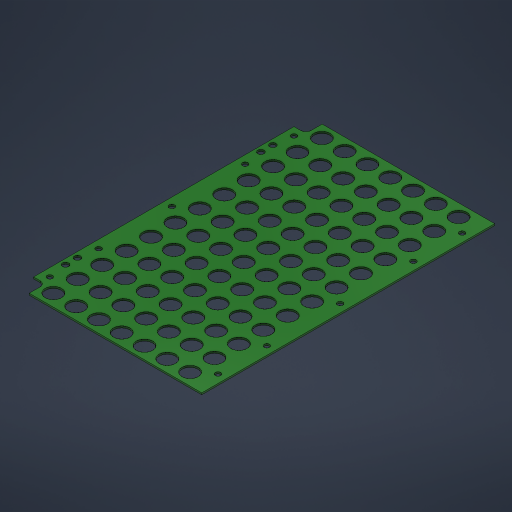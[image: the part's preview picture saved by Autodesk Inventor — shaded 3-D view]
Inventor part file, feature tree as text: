
AUTODESK INVENTOR PART (.ipt)
format: ipt  version: 2023.5 (Build 275446000, 446)  size: 413,696 bytes
history: native  units: mm
features: extrude x2, sketch x2
ambient origin geometry x8: Origin, YZ Plane, XZ Plane, XY Plane, X Axis, Y Axis, Z Axis, Center Point
bodies: Volumenkörper1 (feature_tree)
feature tree (4):
  extrude  "Extrusion1"  Depth=1.6mm
  extrude  "Extrusion2"  Depth=5.0mm
  sketch  "Skizze1"  dims[d0=1.6mm d1=0.0mm d2=5.7mm]
  sketch  "Skizze2"  dims[d3=11.0mm d4=5.0mm d5=39.5mm d6=0.0mm d7=0.0mm]
